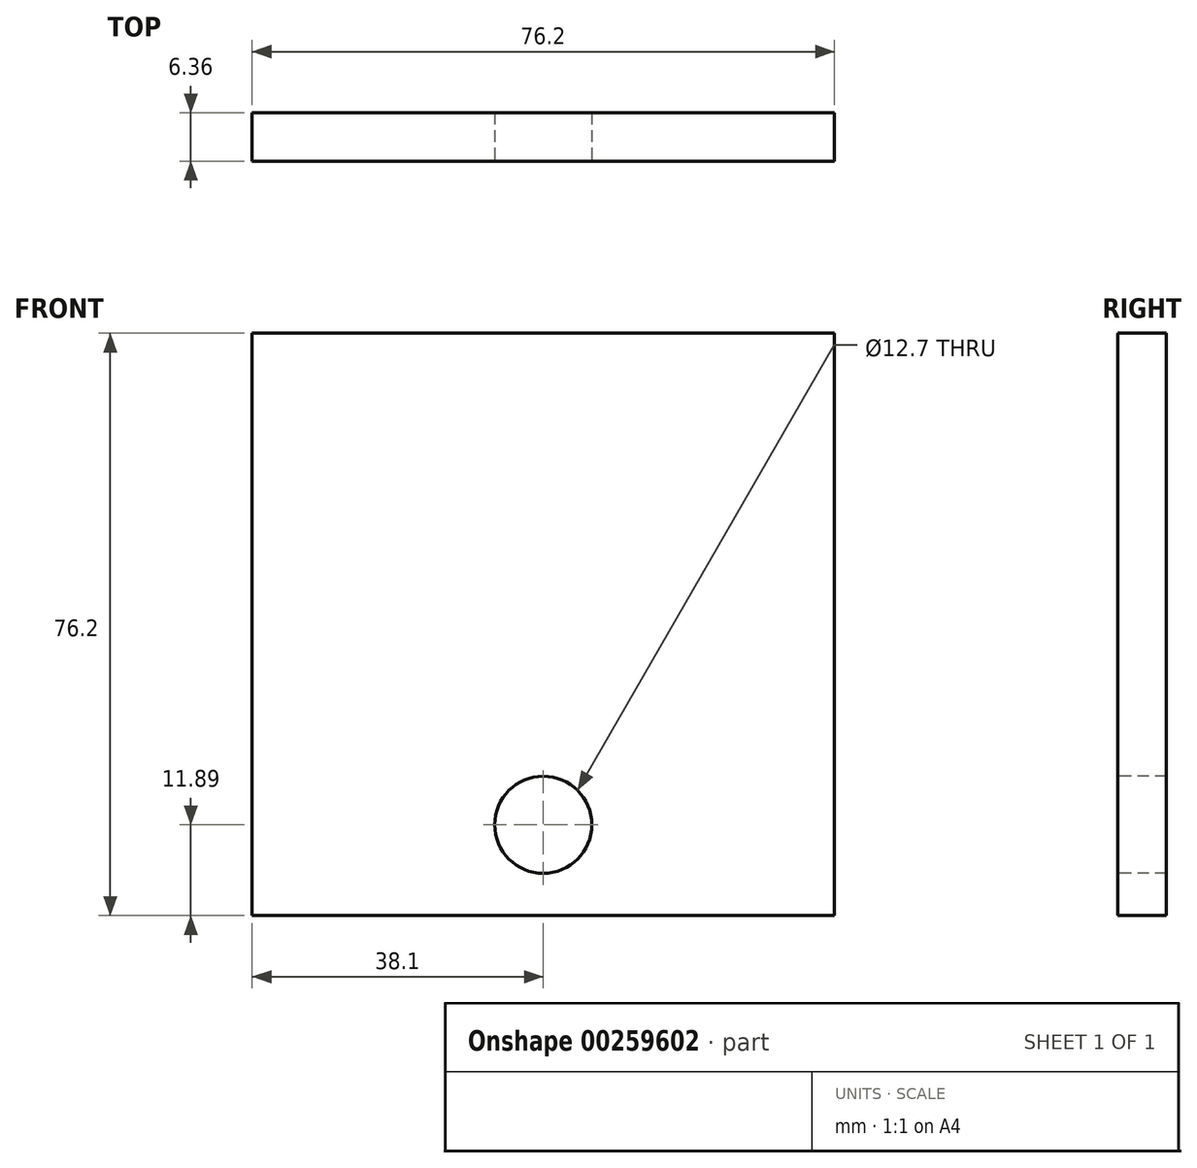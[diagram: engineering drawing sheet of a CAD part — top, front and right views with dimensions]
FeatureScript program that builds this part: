
annotation { "Feature Type Name" : "Feature", "Feature Type Description" : "" }
export const myFeature = defineFeature(function(context is Context, id is Id, definition is map)
    precondition{}
    {
        {
            var Q0;
            Q0=qCreatedBy(makeId("Front.planeOp"),FACE);
            var sketch = newSketch(context, id + "F0", { "sketchPlane" : qUnion([Q0])});
            skLineSegment(sketch, "E0.bottom", {"start": v(38.1, 0) * mm, "end": v(-38.1, 0) * mm});
            skLineSegment(sketch, "E0.top", {"start": v(38.1, 76.2) * mm, "end": v(-38.1, 76.2) * mm});
            skLineSegment(sketch, "E0.left", {"start": v(38.1, 0) * mm, "end": v(38.1, 76.2) * mm});
            skLineSegment(sketch, "E0.right", {"start": v(-38.1, 0) * mm, "end": v(-38.1, 76.2) * mm});
            skSolve(sketch);
        }
        {
            var Q0;
            Q0=makeQuery(id+"F0.imprint","IMPRINT",FACE,{"disambiguationData":[TD([[makeQuery(id+"F0.imprint","IMPRINT",EDGE,{"derivedFrom":sQuery(id+"F0.wireOp",EDGE,"E0.bottom")}),-1.0]])]});
            extrude(context, id + "F1", {"entities" : qUnion([Q0]), "depth" : 6.35 * mm, "symmetric" : true});
        }
        {
            var Q0;
            Q0=makeQuery(id+"F1.opExtrude","CAP_FACE",FACE,{"disambiguationData":[OSD([sQuery(id+"F0.wireOp",EDGE,"E0.bottom"),sQuery(id+"F0.wireOp",EDGE,"E0.top"),sQuery(id+"F0.wireOp",EDGE,"E0.left"),sQuery(id+"F0.wireOp",EDGE,"E0.right")])],"isStart":false});
            var sketch = newSketch(context, id + "F2", { "sketchPlane" : qUnion([Q0])});
            skCircle(sketch, "E1", {"center": v(0, 11.9) * mm, "radius": 6.35 * mm});
            skSolve(sketch);
        }
        {
            var Q0;
            Q0=makeQuery(id+"F2.imprint","IMPRINT",FACE,{"disambiguationData":[TD([[makeQuery(id+"F2.imprint","IMPRINT",EDGE,{"derivedFrom":sQuery(id+"F2.wireOp",EDGE,"E1")}),1.0]])]});
            extrude(context, id + "F3", {"entities" : qUnion([Q0]), "operationType" : NewBodyOperationType.REMOVE, "oppositeDirection" : true, "depth" : 6.35 * mm});
        }
    });
